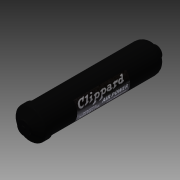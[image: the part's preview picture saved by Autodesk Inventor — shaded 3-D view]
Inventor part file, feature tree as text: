
AUTODESK INVENTOR PART (.ipt)
format: ipt  version: 2016 SP1 (Build 200210100, 210)  size: 186,368 bytes
history: native  units: in
note: dims shown in document units (in); Inventor stores cm internally (conversion verified against a paired STEP export)
features: sketch x8, extrude x4, revolve x3, fillet x2, other x2, projected_geometry x2, plane x1
ambient origin geometry x8: Origin, YZ Plane, XZ Plane, XY Plane, X Axis, Y Axis, Z Axis, Center Point
bodies: Solid1 (feature_tree)
feature tree (22):
  revolve  "Revolution1"  [1 undecoded]
  fillet  "Fillet1"  [1 undecoded]
  revolve  "Revolution2"  [1 undecoded]
  fillet  "Fillet2"  Radius=0.75in
  revolve  "Revolution3"  [1 undecoded]
  extrude  "Extrusion1"  Depth=0.144in TaperAngle=0.0deg
  extrude  "Extrusion2"  Depth=0.1in TaperAngle=0.0deg
  extrude  "Extrusion3"  [1 undecoded]
  extrude  "Extrusion4"  [1 undecoded]
  plane  "Work Plane1"
  other  "Decal1"
  sketch  "Sketch1"  dims[d0=1.28in d1=10.459in d2=90.0deg]
  sketch  "Sketch2"  dims[d3=0.75in d4=1.39in d5=0.75in]
  sketch  "Sketch3"  dims[d6=90.0deg d7=0.25in]
  sketch  "Sketch4"  dims[d8=90.0deg d9=0.144in d10=0.0in]
  projected_geometry  "Projected Loop1"
  sketch  "Sketch5"  dims[d11=0.322in d12=0.0in d13=0.1in d14=0.0in]
  projected_geometry  "Projected Loop2"
  sketch  "Sketch6"  dims[d15=0.1in d16=0.0in]
  sketch  "Sketch7"
  sketch  "Sketch8"
  other  "Image1"
note: 6 required parameter values undecoded (feature->parameter linkage not recoverable at this tier; creation-order binding heuristic only, values carry confidence <= 0.55)